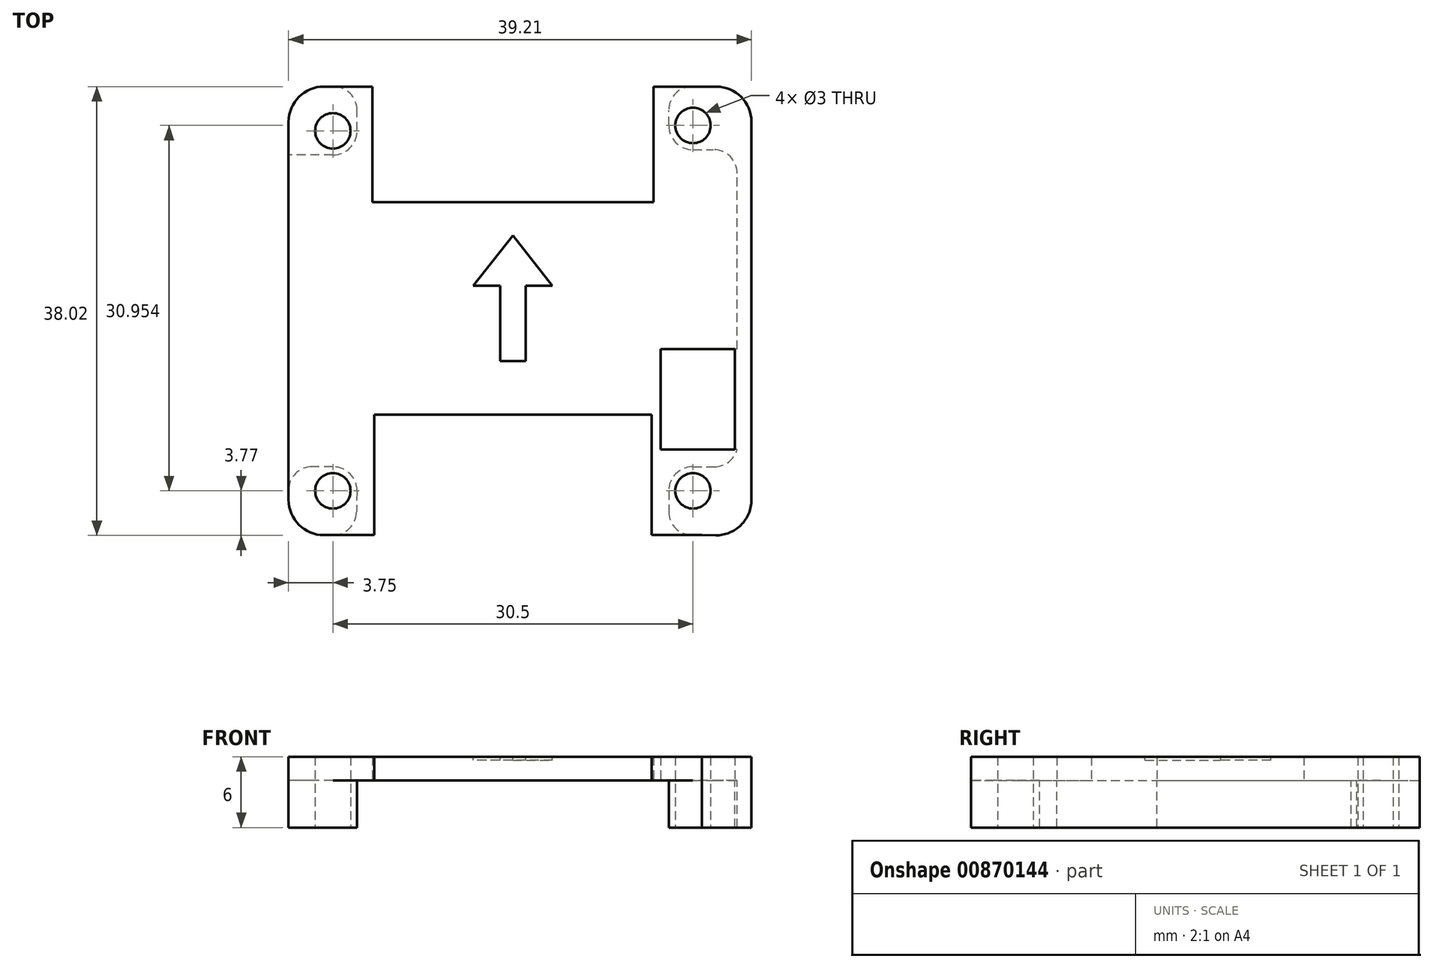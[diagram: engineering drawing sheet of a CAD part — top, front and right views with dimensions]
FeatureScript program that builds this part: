
annotation { "Feature Type Name" : "Feature", "Feature Type Description" : "" }
export const myFeature = defineFeature(function(context is Context, id is Id, definition is map)
    precondition{}
    {
        {
            var Q0;
            Q0=qCreatedBy(makeId("Top.planeOp"),FACE);
            var sketch = newSketch(context, id + "F0", { "sketchPlane" : qUnion([Q0])});
            skLineSegment(sketch, "E0.bottom", {"start": v(16, -19) * mm, "end": v(11.75, -19) * mm});
            skLineSegment(sketch, "E0.top", {"start": v(16, 19) * mm, "end": v(11.9, 19) * mm});
            skLineSegment(sketch, "E0.left", {"start": v(19, -13.2) * mm, "end": v(19, -11.75) * mm});
            skLineSegment(sketch, "E0.right", {"start": v(-19, -16) * mm, "end": v(-19, 16) * mm});
            skPoint(sketch, "E0.middle", {"position": v(0, 0) * mm});
            skPoint(sketch, "E1", {"position": v(15.25, 15.7) * mm});
            skPoint(sketch, "E2", {"position": v(15.25, -15.25) * mm});
            skPoint(sketch, "E3", {"position": v(-15.25, -15.25) * mm});
            skPoint(sketch, "E4", {"position": v(-15.25, 15.25) * mm});
            skCircle(sketch, "E5", {"center": v(-15.25, 15.25) * mm, "radius": 1.5 * mm});
            skCircle(sketch, "E6", {"center": v(15.25, 15.7) * mm, "radius": 1.5 * mm});
            skCircle(sketch, "E7", {"center": v(15.25, -15.25) * mm, "radius": 1.5 * mm});
            skCircle(sketch, "E8", {"center": v(-15.25, -15.25) * mm, "radius": 1.5 * mm});
            skArc(sketch, "E9", {"start": v(-15.25, 13.2) * mm, "mid": v(-13.8, 13.8) * mm, "end": v(-13.2, 15.25) * mm});
            skArc(sketch, "E10", {"start": v(13.2, 15.7) * mm, "mid": v(13.8, 14.25) * mm, "end": v(15.25, 13.65) * mm});
            skArc(sketch, "E11", {"start": v(-13.2, -15.3) * mm, "mid": v(-13.78, -13.82) * mm, "end": v(-15.25, -13.2) * mm});
            skArc(sketch, "E12", {"start": v(15.25, -13.2) * mm, "mid": v(13.8, -13.8) * mm, "end": v(13.2, -15.25) * mm});
            skLineSegment(sketch, "E13", {"start": v(-15.25, 13.2) * mm, "end": v(-19, 13.2) * mm});
            skLineSegment(sketch, "E14", {"start": v(-13.2, 15.25) * mm, "end": v(-13.2, 19) * mm});
            skLineSegment(sketch, "E15", {"start": v(15.25, 13.65) * mm, "end": v(19, 13.65) * mm});
            skLineSegment(sketch, "E16", {"start": v(13.2, 15.7) * mm, "end": v(13.2, 19) * mm});
            skLineSegment(sketch, "E17", {"start": v(-15.25, -13.2) * mm, "end": v(-19, -13.2) * mm});
            skLineSegment(sketch, "E18", {"start": v(-13.2, -15.3) * mm, "end": v(-13.3, -19) * mm});
            skLineSegment(sketch, "E19", {"start": v(15.25, -13.2) * mm, "end": v(19, -13.2) * mm});
            skLineSegment(sketch, "E20", {"start": v(13.2, -15.25) * mm, "end": v(13.2, -19) * mm});
            skPoint(sketch, "E21.visualSharp", {"position": v(-19, 19) * mm});
            skArc(sketch, "E21.filletArc", {"start": v(-16, 19) * mm, "mid": v(-18.12, 18.12) * mm, "end": v(-19, 16) * mm});
            skPoint(sketch, "E22.visualSharp", {"position": v(19, 19) * mm});
            skPoint(sketch, "E23.visualSharp", {"position": v(19, -19) * mm});
            skPoint(sketch, "E24.visualSharp", {"position": v(-19, -19) * mm});
            skArc(sketch, "E24.filletArc", {"start": v(-19, -16) * mm, "mid": v(-18.12, -18.12) * mm, "end": v(-16, -19) * mm});
            skLineSegment(sketch, "E25", {"start": v(0, 9.2) * mm, "end": v(11.9, 9.2) * mm});
            skLineSegment(sketch, "E26", {"start": v(0, 9.2) * mm, "end": v(-11.9, 9.2) * mm});
            skLineSegment(sketch, "E27", {"start": v(-11.9, 9.2) * mm, "end": v(-11.9, 19) * mm});
            skLineSegment(sketch, "E28", {"start": v(11.9, 9.2) * mm, "end": v(11.9, 19) * mm});
            skLineSegment(sketch, "E29.top", {"start": v(11.75, -8.8) * mm, "end": v(-11.75, -8.8) * mm});
            skLineSegment(sketch, "E29.left", {"start": v(11.75, -19) * mm, "end": v(11.75, -8.8) * mm});
            skLineSegment(sketch, "E29.right", {"start": v(-11.75, -19) * mm, "end": v(-11.75, -8.8) * mm});
            skLineSegment(sketch, "E30.bottom", {"start": v(19, -11.75) * mm, "end": v(12.5, -11.75) * mm});
            skLineSegment(sketch, "E30.top", {"start": v(19, -3.25) * mm, "end": v(12.5, -3.25) * mm});
            skLineSegment(sketch, "E30.right", {"start": v(12.5, -11.75) * mm, "end": v(12.5, -3.25) * mm});
            skLineSegment(sketch, "E31.trimOffspring", {"start": v(-11.9, 19) * mm, "end": v(-16, 19) * mm});
            skLineSegment(sketch, "E32.trimOffspring", {"start": v(-11.75, -19) * mm, "end": v(-16, -19) * mm});
            skLineSegment(sketch, "E33.trimOffspring", {"start": v(19, -3.25) * mm, "end": v(19, 13.65) * mm});
            skLineSegment(sketch, "E34", {"start": v(20.2, 19) * mm, "end": v(20.2, -19.05) * mm});
            skLineSegment(sketch, "E35", {"start": v(16, -19) * mm, "end": v(20.2, -19.05) * mm});
            skLineSegment(sketch, "E36", {"start": v(20.2, 19) * mm, "end": v(16, 19) * mm});
            skLineSegment(sketch, "E37", {"start": v(18.8, -3.25) * mm, "end": v(18.8, -11.75) * mm});
            skSolve(sketch);
        }
        {
            var Q0;
            Q0=makeQuery(id+"F0.imprint","IMPRINT",FACE,{"disambiguationData":[TD([[makeQuery(id+"F0.imprint","IMPRINT",EDGE,{"derivedFrom":sQuery(id+"F0.wireOp",EDGE,"E9")}),-1.0]])]});
            var Q1;
            Q1=makeQuery(id+"F0.imprint","IMPRINT",FACE,{"disambiguationData":[TD([[makeQuery(id+"F0.imprint","IMPRINT",EDGE,{"derivedFrom":sQuery(id+"F0.wireOp",EDGE,"E5")}),-1.0]])]});
            var Q2;
            Q2=makeQuery(id+"F0.imprint","IMPRINT",FACE,{"disambiguationData":[TD([[makeQuery(id+"F0.imprint","IMPRINT",EDGE,{"derivedFrom":sQuery(id+"F0.wireOp",EDGE,"E6")}),-1.0]])]});
            var Q3;
            Q3=makeQuery(id+"F0.imprint","IMPRINT",FACE,{"disambiguationData":[TD([[makeQuery(id+"F0.imprint","IMPRINT",EDGE,{"derivedFrom":sQuery(id+"F0.wireOp",EDGE,"E7")}),-1.0]])]});
            var Q4;
            Q4=makeQuery(id+"F0.imprint","IMPRINT",FACE,{"disambiguationData":[TD([[makeQuery(id+"F0.imprint","IMPRINT",EDGE,{"derivedFrom":sQuery(id+"F0.wireOp",EDGE,"E8")}),-1.0]])]});
            extrude(context, id + "F1", {"entities" : qUnion([Q0, Q1, Q2, Q3, Q4]), "depth" : 2 * mm, "offsetDistance" : 25 * mm});
        }
        {
            var Q0;
            Q0=makeQuery(id+"F0.imprint","IMPRINT",FACE,{"disambiguationData":[TD([[makeQuery(id+"F0.imprint","IMPRINT",EDGE,{"derivedFrom":sQuery(id+"F0.wireOp",EDGE,"E8")}),-1.0]])]});
            var Q1;
            Q1=makeQuery(id+"F0.imprint","IMPRINT",FACE,{"disambiguationData":[TD([[makeQuery(id+"F0.imprint","IMPRINT",EDGE,{"derivedFrom":sQuery(id+"F0.wireOp",EDGE,"E7")}),-1.0]])]});
            var Q2;
            Q2=makeQuery(id+"F0.imprint","IMPRINT",FACE,{"disambiguationData":[TD([[makeQuery(id+"F0.imprint","IMPRINT",EDGE,{"derivedFrom":sQuery(id+"F0.wireOp",EDGE,"E6")}),-1.0]])]});
            var Q3;
            Q3=makeQuery(id+"F0.imprint","IMPRINT",FACE,{"disambiguationData":[TD([[makeQuery(id+"F0.imprint","IMPRINT",EDGE,{"derivedFrom":sQuery(id+"F0.wireOp",EDGE,"E5")}),-1.0]])]});
            extrude(context, id + "F2", {"entities" : qUnion([Q0, Q1, Q2, Q3]), "operationType" : NewBodyOperationType.ADD, "oppositeDirection" : true, "depth" : 4 * mm, "offsetDistance" : 25 * mm});
        }
        {
            var Q0;
            Q0=makeQuery(id+"F2.opExtrude","SWEPT_EDGE",EDGE,{"disambiguationData":[OSD([sQuery(id+"F0.wireOp",EDGE,"E14"),sQuery(id+"F0.wireOp",EDGE,"E31.trimOffspring")])]});
            fillet(context, id + "F3", {"entities" : qUnion([Q0]), "radius" : 2 * mm, "tangentPropagation" : true, "allowEdgeOverflow" : false});
        }
        {
            var Q0;
            Q0=makeQuery(id+"F2.opExtrude","SWEPT_EDGE",EDGE,{"disambiguationData":[OSD([sQuery(id+"F0.wireOp",EDGE,"E0.top"),sQuery(id+"F0.wireOp",EDGE,"E16")])]});
            var Q1;
            Q1=makeQuery(id+"F2.opExtrude","SWEPT_EDGE",EDGE,{"disambiguationData":[OSD([sQuery(id+"F0.wireOp",EDGE,"E15"),sQuery(id+"F0.wireOp",EDGE,"E33.trimOffspring")])]});
            var Q2;
            Q2=makeQuery(id+"F2.opExtrude","SWEPT_EDGE",EDGE,{"disambiguationData":[OSD([sQuery(id+"F0.wireOp",EDGE,"E0.left"),sQuery(id+"F0.wireOp",EDGE,"E19")])]});
            var Q3;
            Q3=makeQuery(id+"F2.opExtrude","SWEPT_EDGE",EDGE,{"disambiguationData":[OSD([sQuery(id+"F0.wireOp",EDGE,"E0.bottom"),sQuery(id+"F0.wireOp",EDGE,"E20")])]});
            var Q4;
            Q4=makeQuery(id+"F2.opExtrude","SWEPT_EDGE",EDGE,{"disambiguationData":[OSD([sQuery(id+"F0.wireOp",EDGE,"E18"),sQuery(id+"F0.wireOp",EDGE,"E32.trimOffspring")])]});
            var Q5;
            Q5=makeQuery(id+"F2.opExtrude","SWEPT_EDGE",EDGE,{"disambiguationData":[OSD([sQuery(id+"F0.wireOp",EDGE,"E0.right"),sQuery(id+"F0.wireOp",EDGE,"E17")])]});
            fillet(context, id + "F4", {"entities" : qUnion([Q0, Q1, Q2, Q3, Q4, Q5]), "radius" : 2 * mm, "tangentPropagation" : true, "allowEdgeOverflow" : false});
        }
        {
            var Q0;
            {var subQ0=sQuery(id+"F0.wireOp",EDGE,"E35");var subQ1=sQuery(id+"F0.wireOp",EDGE,"E34");Q0=makeQuery(id+"F2.boolean.opBoolean","MERGE",EDGE,{"derivedFrom":[makeQuery(id+"F1.opExtrude","SWEPT_EDGE",EDGE,{"disambiguationData":[OSD([subQ1,subQ0])]}),makeQuery(id+"F2.opExtrude","SWEPT_EDGE",EDGE,{"disambiguationData":[OSD([subQ1,subQ0])]})]});}
            fillet(context, id + "F5", {"entities" : qUnion([Q0]), "radius" : 3 * mm, "tangentPropagation" : true, "allowEdgeOverflow" : false});
        }
        {
            var Q0;
            {var subQ0=sQuery(id+"F0.wireOp",EDGE,"E36");var subQ1=sQuery(id+"F0.wireOp",EDGE,"E34");Q0=makeQuery(id+"F2.boolean.opBoolean","MERGE",EDGE,{"derivedFrom":[makeQuery(id+"F1.opExtrude","SWEPT_EDGE",EDGE,{"disambiguationData":[OSD([subQ1,subQ0])]}),makeQuery(id+"F2.opExtrude","SWEPT_EDGE",EDGE,{"disambiguationData":[OSD([subQ1,subQ0])]})]});}
            fillet(context, id + "F6", {"entities" : qUnion([Q0]), "radius" : 3 * mm, "tangentPropagation" : true, "allowEdgeOverflow" : false});
        }
        {
            var Q0;
            Q0=makeQuery(id+"F1.opExtrude","CAP_FACE",FACE,{"disambiguationData":[OSD([sQuery(id+"F0.wireOp",EDGE,"E0.bottom"),sQuery(id+"F0.wireOp",EDGE,"E0.top"),sQuery(id+"F0.wireOp",EDGE,"E0.right"),sQuery(id+"F0.wireOp",EDGE,"E5"),sQuery(id+"F0.wireOp",EDGE,"E6"),sQuery(id+"F0.wireOp",EDGE,"E7"),sQuery(id+"F0.wireOp",EDGE,"E8"),sQuery(id+"F0.wireOp",EDGE,"E21.filletArc"),sQuery(id+"F0.wireOp",EDGE,"E24.filletArc"),sQuery(id+"F0.wireOp",EDGE,"E25"),sQuery(id+"F0.wireOp",EDGE,"E26"),sQuery(id+"F0.wireOp",EDGE,"E27"),sQuery(id+"F0.wireOp",EDGE,"E28"),sQuery(id+"F0.wireOp",EDGE,"E29.top"),sQuery(id+"F0.wireOp",EDGE,"E29.left"),sQuery(id+"F0.wireOp",EDGE,"E29.right"),sQuery(id+"F0.wireOp",EDGE,"E30.bottom"),sQuery(id+"F0.wireOp",EDGE,"E30.top"),sQuery(id+"F0.wireOp",EDGE,"E30.right"),sQuery(id+"F0.wireOp",EDGE,"E31.trimOffspring"),sQuery(id+"F0.wireOp",EDGE,"E32.trimOffspring"),sQuery(id+"F0.wireOp",EDGE,"E34"),sQuery(id+"F0.wireOp",EDGE,"E35"),sQuery(id+"F0.wireOp",EDGE,"E36"),sQuery(id+"F0.wireOp",EDGE,"E37")])],"isStart":false});
            var sketch = newSketch(context, id + "F7", { "sketchPlane" : qUnion([Q0])});
            skLineSegment(sketch, "E38.bottom", {"start": v(1.07, -4.26) * mm, "end": v(-1.07, -4.26) * mm});
            skLineSegment(sketch, "E38.left", {"start": v(1.07, -4.26) * mm, "end": v(1.07, 2.13) * mm});
            skLineSegment(sketch, "E38.right", {"start": v(-1.07, -4.26) * mm, "end": v(-1.07, 2.13) * mm});
            skPoint(sketch, "E38.middle", {"position": v(0, 0) * mm});
            skLineSegment(sketch, "E39.bottom", {"start": v(3.35, 2.13) * mm, "end": v(1.07, 2.13) * mm});
            skPoint(sketch, "E39.middle", {"position": v(0, 4.26) * mm});
            skLineSegment(sketch, "E40", {"start": v(0, 6.39) * mm, "end": v(-3.35, 2.13) * mm});
            skLineSegment(sketch, "E41", {"start": v(0, 6.39) * mm, "end": v(3.35, 2.13) * mm});
            skPoint(sketch, "E39.right.end.orphan", {"position": v(-3.35, 6.39) * mm});
            skPoint(sketch, "E39.left.end.orphan", {"position": v(3.35, 6.39) * mm});
            skPoint(sketch, "E42.orphan", {"position": v(-1.07, 4.26) * mm});
            skPoint(sketch, "E38.top.start.orphan", {"position": v(1.07, 4.26) * mm});
            skLineSegment(sketch, "E43.trimOffspring", {"start": v(-1.07, 2.13) * mm, "end": v(-3.35, 2.13) * mm});
            skSolve(sketch);
        }
        {
            var Q0;
            Q0=makeQuery(id+"F7.imprint","IMPRINT",FACE,{"disambiguationData":[TD([[makeQuery(id+"F7.imprint","IMPRINT",EDGE,{"derivedFrom":sQuery(id+"F7.wireOp",EDGE,"E38.bottom")}),-1.0]])]});
            extrude(context, id + "F8", {"entities" : qUnion([Q0]), "operationType" : NewBodyOperationType.REMOVE, "oppositeDirection" : true, "depth" : 0.3 * mm, "offsetDistance" : 25 * mm});
        }
    });
